# Revit family: ASH_ArmitageShanks_WCSeats_Contour21_S4065
name_source: partatom
category: Plumbing Fixtures
revit_build: Autodesk Revit MEP 2012 (Build: 20110309_2315(x64)
units: mm (PartAtom-declared; Revit-internal decimal feet)

## types (4) — shared parameters
AccessibilityPerformance = DDA Compliant
Accessories = www.idealspec.co.uk
AreaUnits = millimeters
Assembly Code = C1030200
AssetType = Fixed
Brand = Armitage Shanks
CodePerformance = DDA Compliant
ConnectionType = Mechanical
Description = Contour 21 seat and cover, top fixing hinges
DurationUnit = year
ECA = No
ExpectedLife = 15
Features = Seat & cover, top fixing hinges
Help = www.idealspec.co.uk/contact-us.html
IfcExportAs = IfcSanitaryTerminalType
IfcExportType = WCSEAT
InstallationInstructions = www.idealspec.co.uk/resources.html
LinearUnits = millimeters
ManufacturerURL = www.idealspec.co.uk
Material = Plastic
ModelReference = Contour 21 seat and cover, top fixing hinges
NBSDescription = WC seats and covers
NBSReference = 45-35-70/391
Name = WCSeats_Contour21-Seat&Cover-S4065_ArmitageShanks
NettWeight = 1.5Kg
NominalDepth = 409 mm
NominalHeight = 45 mm
NominalLength = 409 mm
NominalWidth = 380 mm  [stored 1.24672 ft]
ProductInformation = www.idealspec.co.uk/assets/datasheet/S406501
SeatColor = White
SeatHasCover = Yes
SeatMaterial = Plastic
SeatType = RingSeat
Shape = Ring
Space = Internal
SpareParts = www.fastpart-spares.co.uk
URL = www.idealspec.co.uk
Uniclass2 = Pr_40_20_93_95
Version = 2
VolumeUnits = Litres
WRAS = No
WarrantyDescription = Manufacturers Warranty
WarrantyDurationParts = 5
WarrantyDurationUnit = year
WaterEfficientProduct = No
zero-valued in all types: CWFU, Default Elevation, HWFU, WFU

## per-type parameters (varying)
| type | BIMObjectName | Finish | Model | ModelNumber | SeatSKU | Size |
| S406501 - Contour 21 Seat & Cover | ASH_ArmitageShanks_WCSeats_Contour21-Seat&Cover_S406501 | White 01 | S406501 | S406501 | ASH_ArmitageShanks _WC_White2_Render | x x mm |
| S4065LJ - Contour 21 Seat & Cover | ASH_ArmitageShanks_WCSeats_Contour21-Seat&Cover_S4065LJ | Grey LJ | S4065LJ | S4065LJ | ASH_ArmitageShanks _WC_GreyLJ_Render | x x mm |
| S406536 - Contour 21 Seat & Cover | ASH_ArmitageShanks_WCSeats_Contour21-Seat&Cover_S4065 | Blue 36 | S406536 | S406536 | ASH_ArmitageShanks _WC_Blue36_Render | x x mm |
| S4065RN - Contour 21 Seat & Cover | ASH_ArmitageShanks_WCSeats_Contour21-Seat&Cover_S4065RN | Charcoal RN | S4065RN | S4065RN | ASH_ArmitageShanks _WC_CharcoalRN_Render | 410 x 380 x 45 mm |

note: [stored X ft] marks values corroborated as IEEE doubles in the binary element streams (Revit-internal decimal feet)

## geometry (parser evidence)
native form markers: Sweep x3
no freeform markers — native parametric forms only
